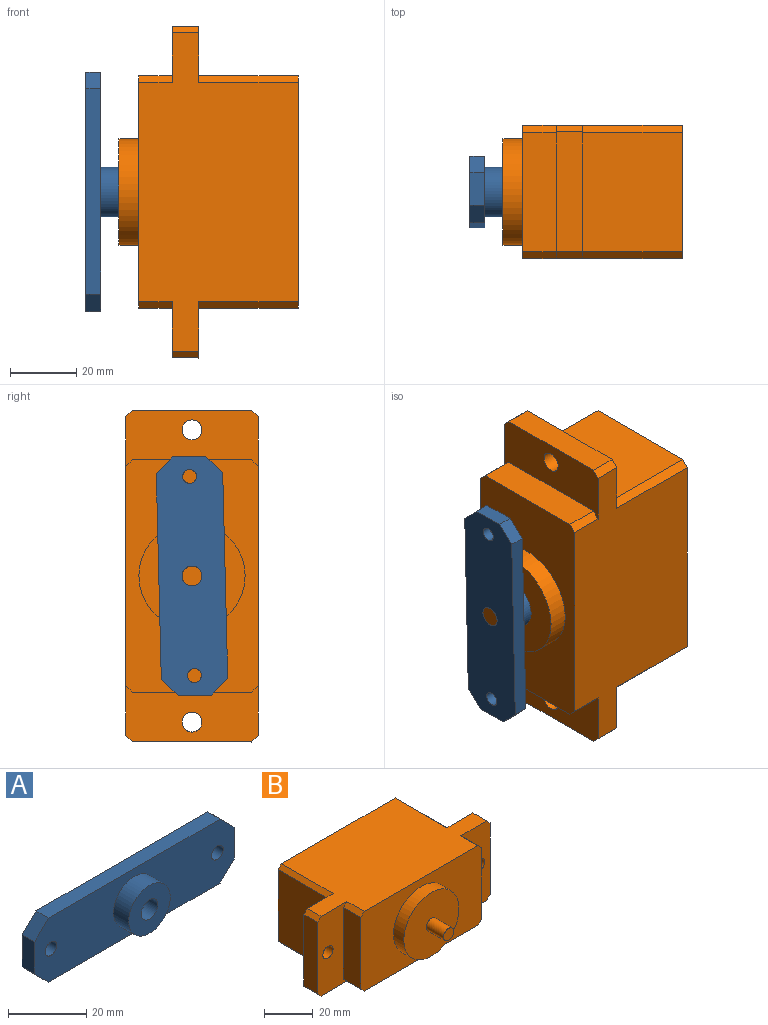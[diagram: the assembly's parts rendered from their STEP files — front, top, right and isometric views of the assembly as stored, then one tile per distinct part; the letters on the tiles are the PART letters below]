
ASSEMBLY  parts=2 mates=1
PART A: 15 faces, bbox 72x10x20 mm
  f0: plane 62x4.5mm, normal (0,0,-1), area 279mm2, adj f5,f6,f9,f11
  f1: plane 10x4.5mm, normal (1,0,0), area 45mm2, adj f5,f6,f11,f12
  f2: plane 62x4.5mm, normal (0,0,1), area 279mm2, adj f5,f6,f10,f12
  f3: cylinder r=3mm len=10mm, axis (0,1,0), area 188.5mm2, adj f6,f8
  f4: plane 10x4.5mm, normal (-1,0,0), area 45mm2, adj f5,f6,f9,f10
  f5: plane 72x20mm, normal (0,-1,0), area 1185.6mm2, adj f0,f1,f2,f4,f7,f9,f10,f11
  f6: plane 72x20mm, normal (0,1,0), area 1334mm2, adj f0,f1,f2,f3,f4,f9,f10,f11
  f7: cylinder r=7.5mm len=15mm, axis (0,1,0), area 259.2mm2, adj f5,f8
  f8: plane 15x15mm, normal (0,-1,0), area 148.4mm2, adj f3,f7
  f9: plane 5x5mm, normal (-0.71,0,-0.71), area 31.8mm2, adj f0,f4,f5,f6
  f10: plane 5x5mm, normal (-0.71,0,0.71), area 31.8mm2, adj f2,f4,f5,f6
  f11: plane 5x5mm, normal (0.71,0,-0.71), area 31.8mm2, adj f0,f1,f5,f6
  f12: plane 5x5mm, normal (0.71,0,0.71), area 31.8mm2, adj f1,f2,f5,f6
  f13: cylinder r=2.1mm len=4.5mm, axis (0,1,0), area 59.4mm2, adj f5,f6
  f14: cylinder r=2.1mm len=4.5mm, axis (0,1,0), area 59.4mm2, adj f5,f6
PART B: 32 faces, bbox 100x64x40 mm
  f0: plane 40x17mm, normal (0,-1,0), area 571.7mm2, adj f1,f11,f12,f13,f21,f22,f23,f24
  f1: plane 36x8mm, normal (1,0,0), area 288mm2, adj f0,f2,f21,f23
  f2: plane 40x17mm, normal (0,1,0), area 571.7mm2, adj f1,f3,f12,f13,f20,f21,f23,f25
  f3: plane 36x30mm, normal (1,0,0), area 1080mm2, adj f2,f4,f20,f25
  f4: plane 70x40mm, normal (0,1,0), area 2792mm2, adj f3,f5,f12,f13,f16,f19,f20,f25
  f5: plane 36x30mm, normal (-1,0,0), area 1080mm2, adj f4,f6,f16,f19
  f6: plane 40x17mm, normal (0,1,0), area 571.7mm2, adj f5,f7,f12,f13,f15,f16,f17,f19
  f7: plane 36x8mm, normal (-1,0,0), area 288mm2, adj f6,f8,f15,f17
  f8: plane 40x17mm, normal (0,-1,0), area 571.7mm2, adj f7,f9,f12,f13,f14,f15,f17,f18
  f9: plane 36x10mm, normal (-1,0,0), area 360mm2, adj f8,f10,f14,f18
  f10: plane 70x40mm, normal (0,-1,0), area 1987.8mm2, adj f9,f11,f12,f13,f14,f18,f22,f24
  f11: plane 36x10mm, normal (1,0,0), area 360mm2, adj f0,f10,f22,f24
  f12: plane 96x48mm, normal (0,0,1), area 3408mm2, adj f0,f2,f4,f6,f8,f10,f17,f18
  f13: plane 96x48mm, normal (0,0,-1), area 3408mm2, adj f0,f2,f4,f6,f8,f10,f14,f15
  f14: plane 10x2mm, normal (-0.71,0,-0.71), area 28.3mm2, adj f8,f9,f10,f13
  f15: plane 8x2mm, normal (-0.71,0,-0.71), area 22.6mm2, adj f6,f7,f8,f13
  f16: plane 30x2mm, normal (-0.71,0,-0.71), area 84.9mm2, adj f4,f5,f6,f13
  f17: plane 8x2mm, normal (-0.71,0,0.71), area 22.6mm2, adj f6,f7,f8,f12
  f18: plane 10x2mm, normal (-0.71,0,0.71), area 28.3mm2, adj f8,f9,f10,f12
  f19: plane 30x2mm, normal (-0.71,0,0.71), area 84.9mm2, adj f4,f5,f6,f12
  f20: plane 30x2mm, normal (0.71,0,-0.71), area 84.9mm2, adj f2,f3,f4,f13
  f21: plane 8x2mm, normal (0.71,0,-0.71), area 22.6mm2, adj f0,f1,f2,f13
  f22: plane 10x2mm, normal (0.71,0,-0.71), area 28.3mm2, adj f0,f10,f11,f13
  f23: plane 8x2mm, normal (0.71,0,0.71), area 22.6mm2, adj f0,f1,f2,f12
  f24: plane 10x2mm, normal (0.71,0,0.71), area 28.3mm2, adj f0,f10,f11,f12
  f25: plane 30x2mm, normal (0.71,0,0.71), area 84.9mm2, adj f2,f3,f4,f12
  f26: cylinder r=16mm len=32mm, axis (0,1,0), area 603.2mm2, adj f10,f27
  f27: plane 32x32mm, normal (0,-1,0), area 776mm2, adj f26,f28
  f28: cylinder r=3mm len=10mm, axis (0,1,0), area 188.5mm2, adj f27,f29
  f29: plane 6x6mm, normal (0,-1,0), area 28.3mm2, adj f28
  f30: cylinder r=3mm len=8mm, axis (0,-1,0), area 150.8mm2, adj f6,f8
  f31: cylinder r=3mm len=8mm, axis (0,-1,0), area 150.8mm2, adj f0,f2
PLACE A rot(axis=(0.57,-0.57,0.59),119.2deg) t=(-233.2,-117.19,45.22)mm
PLACE B rot(axis=(0.58,0.58,-0.58),120deg) t=(-199.2,-97.19,45.22)mm fixed
MATE revolute A.f3 <-> B.f26  axis (-1,0,0) through (-233.2,-117.19,45.22)mm
